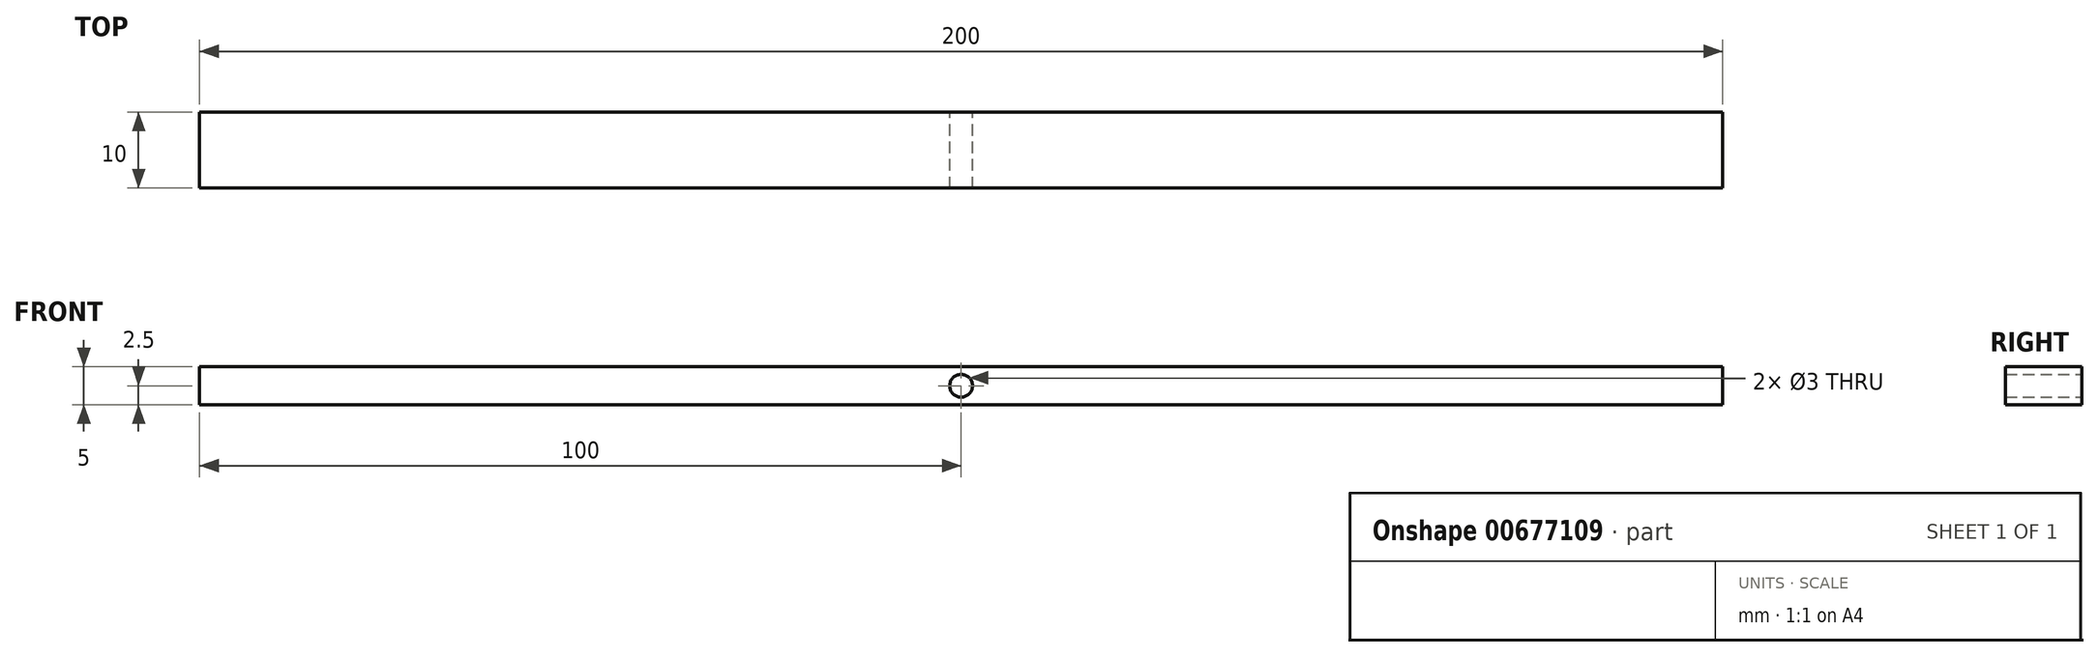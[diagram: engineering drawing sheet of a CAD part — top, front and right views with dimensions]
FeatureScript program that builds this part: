
annotation { "Feature Type Name" : "Feature", "Feature Type Description" : "" }
export const myFeature = defineFeature(function(context is Context, id is Id, definition is map)
    precondition{}
    {
        {
            var Q0;
            Q0=qCreatedBy(makeId("Front.planeOp"),FACE);
            var sketch = newSketch(context, id + "F0", { "sketchPlane" : qUnion([Q0])});
            skLineSegment(sketch, "E0.bottom", {"start": v(100, -2.5) * mm, "end": v(-100, -2.5) * mm});
            skLineSegment(sketch, "E0.top", {"start": v(100, 2.5) * mm, "end": v(-100, 2.5) * mm});
            skLineSegment(sketch, "E0.left", {"start": v(100, -2.5) * mm, "end": v(100, 2.5) * mm});
            skLineSegment(sketch, "E0.right", {"start": v(-100, -2.5) * mm, "end": v(-100, 2.5) * mm});
            skPoint(sketch, "E0.middle", {"position": v(0, 0) * mm});
            skCircle(sketch, "E1", {"center": v(0, 0) * mm, "radius": 1.5 * mm});
            skSolve(sketch);
        }
        {
            var Q0;
            Q0=makeQuery(id+"F0.imprint","IMPRINT",FACE,{"disambiguationData":[TD([[makeQuery(id+"F0.imprint","IMPRINT",EDGE,{"derivedFrom":sQuery(id+"F0.wireOp",EDGE,"E0.bottom")}),-1.0]])]});
            extrude(context, id + "F1", {"entities" : qUnion([Q0]), "endBound" : BoundingType.SYMMETRIC, "depth" : 10 * mm, "offsetDistance" : 25 * mm});
        }
        {
            var Q0;
            Q0=makeQuery(id+"F1.opExtrude","SWEPT_BODY",BODY,{"disambiguationData":[OSD([sQuery(id+"F0.wireOp",EDGE,"E0.bottom"),sQuery(id+"F0.wireOp",EDGE,"E0.top"),sQuery(id+"F0.wireOp",EDGE,"E0.left"),sQuery(id+"F0.wireOp",EDGE,"E0.right"),sQuery(id+"F0.wireOp",EDGE,"E1")])]});
            transform(context, id + "F2", {"entities" : qUnion([Q0]), "transformType" : TransformType.TRANSLATION_3D, "dx" : 0 * mm, "dy" : 0 * mm, "dz" : 0 * mm, "makeCopy" : true});
        }
    });
